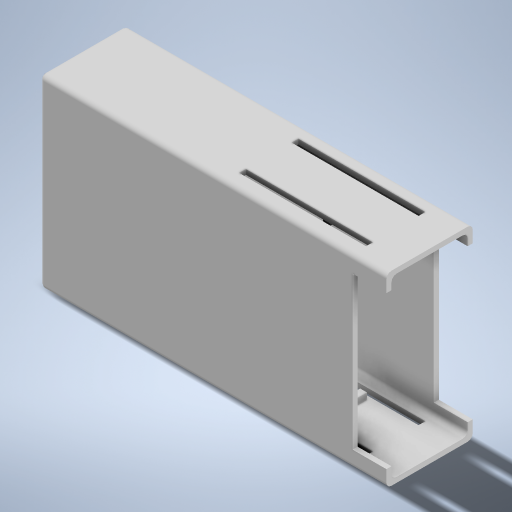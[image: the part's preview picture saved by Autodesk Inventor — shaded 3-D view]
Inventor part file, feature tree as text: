
AUTODESK INVENTOR PART (.ipt)
format: ipt  version: 2023.3 (Build 273359000, 359)  size: 355,840 bytes
history: native  units: mm
features: extrude x7, sketch x7, projected_geometry x2, fillet x1
ambient origin geometry x8: Origin, YZ Plane, XZ Plane, XY Plane, X Axis, Y Axis, Z Axis, Center Point
bodies: Solid1 (feature_tree)
feature tree (17):
  extrude  "Extrusion1"  Depth=18.5mm
  extrude  "Extrusion2"  Depth=0.3mm
  extrude  "Extrusion3"  Depth=0.3mm
  extrude  "Extrusion4"  Depth=0.3mm TaperAngle=0.0deg
  extrude  "Extrusion5"  Depth=2.3mm
  fillet  "Fillet1"  Radius=1.8mm
  extrude  "Extrusion6"  Depth=10.0mm TaperAngle=0.0deg
  extrude  "Extrusion7"  Depth=0.4mm
  sketch  "Sketch1"  dims[d0=0.3mm d1=18.5mm]
  sketch  "Sketch2"  dims[d2=10.4mm d3=0.3mm]
  sketch  "Sketch3"  dims[d4=5.1mm d5=0.0mm d6=0.3mm]
  sketch  "Sketch4"  dims[d7=0.3mm d8=5.0mm d9=0.0mm]
  sketch  "Sketch5"  dims[d10=2.3mm d11=2.3mm d12=1.8mm]
  projected_geometry  "Projected Loop1"
  sketch  "Sketch6"  dims[d13=3.5mm d14=10.0mm d15=0.0mm]
  sketch  "Sketch7"  dims[d16=15.0mm d17=0.4mm d18=2.2mm d19=0.4mm d20=0.0mm d21=0.4mm d22=0.0mm d23=0.3mm d24=1.0mm d25=1.0mm d26=1.0mm d27=1.0mm d28=2.0mm d29=0.0mm d30=2.0mm d31=0.25mm d32=0.25mm d33=0.4mm d34=7.5mm d35=0.4mm d36=0.0mm]
  projected_geometry  "Projected Loop2"
